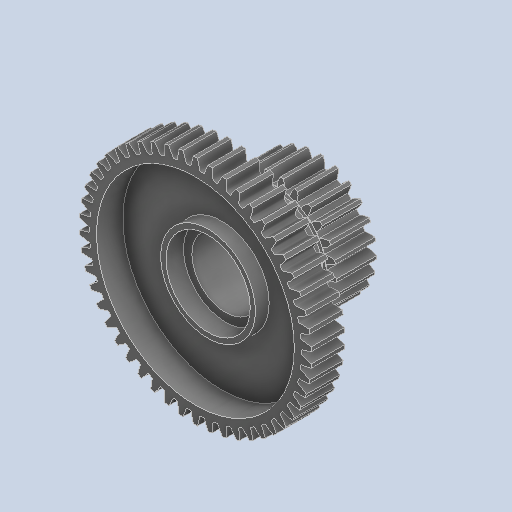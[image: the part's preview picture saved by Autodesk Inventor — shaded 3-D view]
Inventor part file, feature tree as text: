
AUTODESK INVENTOR PART (.ipt)
format: ipt  version: 2023.2 (Build 272271000, 271)  size: 584,704 bytes
history: native  units: in
note: dims shown in document units (in); Inventor stores cm internally (conversion verified against a paired STEP export)
features: chamfer x1
ambient origin geometry x8: Origin, YZ Plane, XZ Plane, XY Plane, X Axis, Y Axis, Z Axis, Center Point
bodies: Solid1 (feature_tree)
feature tree (1):
  chamfer  "Chamfer2"  [1 undecoded]
note: 1 required parameter value undecoded (feature->parameter linkage not recoverable at this tier; creation-order binding heuristic only, values carry confidence <= 0.55)
